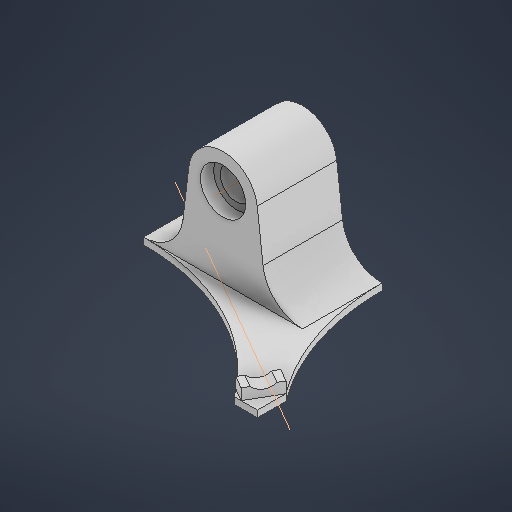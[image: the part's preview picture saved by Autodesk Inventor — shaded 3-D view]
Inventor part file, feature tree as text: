
AUTODESK INVENTOR PART (.ipt)
format: ipt  version: 2025.3 (Build 293356030, 356C)  size: 285,184 bytes
history: native  units: mm
features: extrude x7, sketch x4, other x2, plane x2, projected_geometry x1
ambient origin geometry x8: Origin, YZ Plane, XZ Plane, XY Plane, X Axis, Y Axis, Z Axis, Center Point
bodies: Body1 (feature_tree)
feature tree (16):
  sketch  "Sketch1"  dims[d2=17.05mm d3=12.0mm]
  extrude  "Extrusion3"  Depth=12.0mm
  extrude  "Extrusion4"  Depth=13.0mm
  other  "Work Axis1"
  extrude  "Extrusion5"  Depth=60.0mm
  extrude  "Extrusion6"  Depth=30.0mm TaperAngle=0.0deg
  plane  "Work Plane1"
  plane  "Work Plane3"
  extrude  "Extrusion9"  Depth=20.0mm TaperAngle=0.0deg
  other  "Work Axis3"
  extrude  "Extrusion10"  Depth=15.0mm TaperAngle=0.0deg
  extrude  "Extrusion11"  Depth=5.5mm TaperAngle=0.0deg
  sketch  "Sketch5"  dims[d9=30.0mm d12=13.0mm]
  sketch  "Sketch6"  dims[d15=15.0mm d16=60.0mm]
  projected_geometry  "Projected Loop1"
  sketch  "Sketch7"  dims[d17=2.5mm d18=30.0mm d19=0.0mm d20=20.0mm d21=0.0mm d22=15.0mm d23=0.0mm d24=50.0mm d25=0.0mm d26=60.0deg d45=7.5mm d46=12.0mm d47=10.7mm d48=14.6mm d49=8.0mm d51=1.5mm d52=5.5mm d53=0.0mm d54=18.0mm d55=0.0mm d56=0.0mm d57=0.0mm d30=0.5mm d31=0.872665mm d32=0.5mm d33=0.872665mm]
